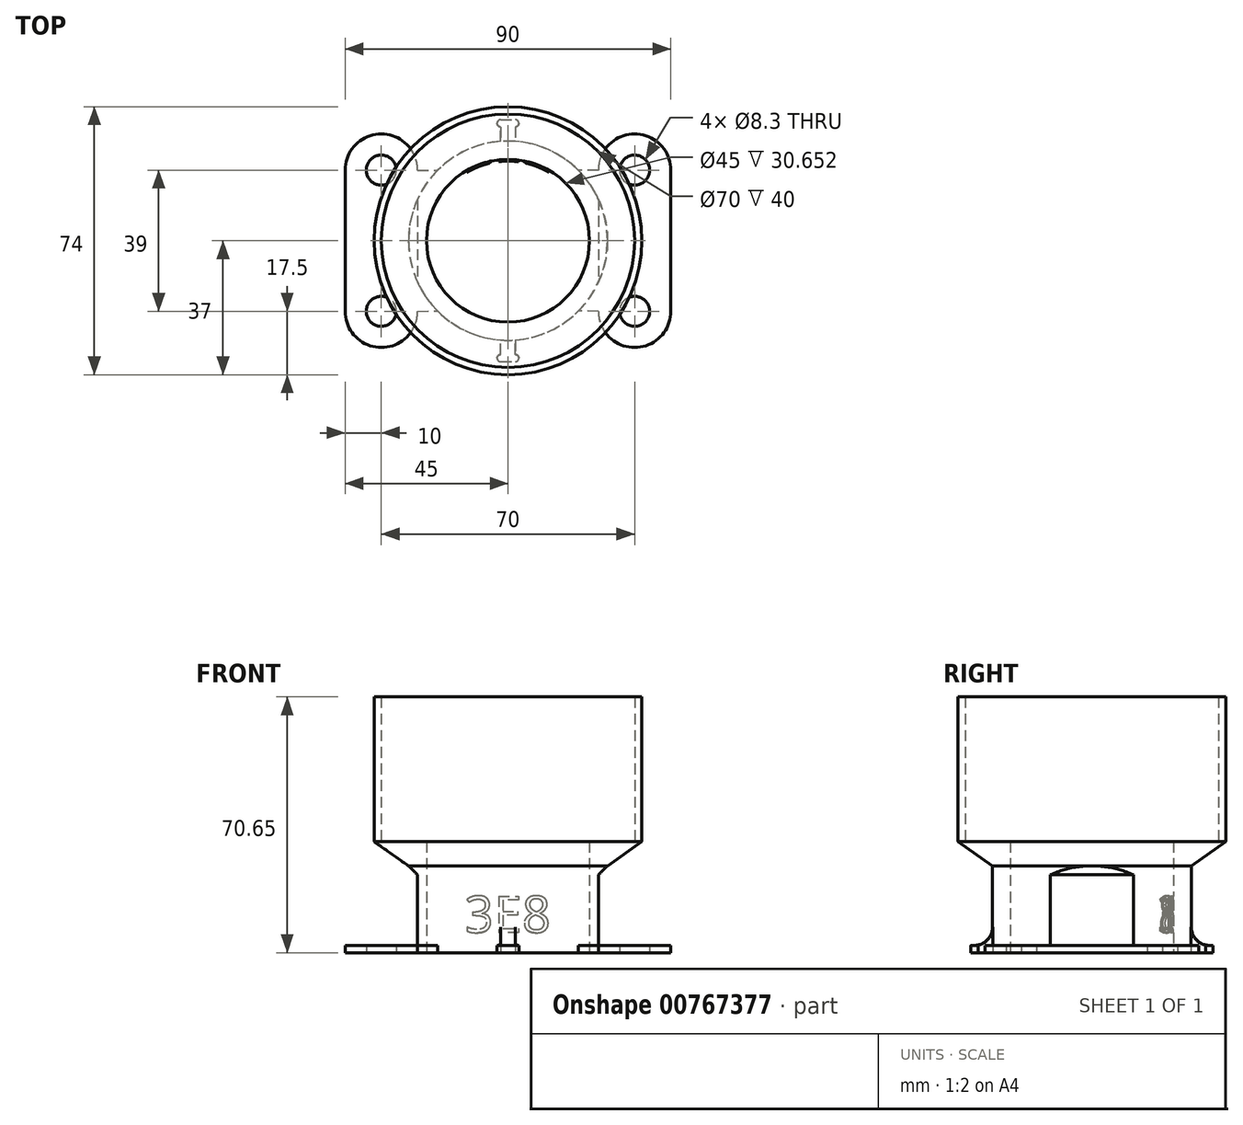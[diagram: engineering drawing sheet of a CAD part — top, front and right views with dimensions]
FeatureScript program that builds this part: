
annotation { "Feature Type Name" : "Feature", "Feature Type Description" : "" }
export const myFeature = defineFeature(function(context is Context, id is Id, definition is map)
    precondition{}
    {
        {
            assignVariable(context, id + "F0", {"name" : "mountheight", "anyValue" : 22});
        }
        {
            assignVariable(context, id + "F1", {"name" : "cupholderdepth", "anyValue" : 40});
        }
        {
            var Q0;
            Q0=qCreatedBy(makeId("Top.planeOp"),FACE);
            var sketch = newSketch(context, id + "F2", { "sketchPlane" : qUnion([Q0])});
            skLineSegment(sketch, "E0", {"start": v(-35, 0) * mm, "end": v(35, 0) * mm, "construction": true});
            skLineSegment(sketch, "E1", {"start": v(0, 27.5) * mm, "end": v(0, 0) * mm, "construction": true});
            skLineSegment(sketch, "E2", {"start": v(-35, 19.5) * mm, "end": v(-35, -19.5) * mm, "construction": true});
            skCircle(sketch, "E3", {"center": v(-35, 19.5) * mm, "radius": 4.15 * mm});
            skCircle(sketch, "E4.MirrorC", {"center": v(-35, -19.5) * mm, "radius": 4.15 * mm});
            skCircle(sketch, "E5.MirrorC", {"center": v(35, 19.5) * mm, "radius": 4.15 * mm});
            skCircle(sketch, "E6.MirrorC", {"center": v(35, -19.5) * mm, "radius": 4.15 * mm});
            skCircle(sketch, "E7", {"center": v(-35, 19.5) * mm, "radius": 10 * mm, "construction": true});
            skCircle(sketch, "E8.MirrorC", {"center": v(-35, -19.5) * mm, "radius": 10 * mm, "construction": true});
            skLineSegment(sketch, "E9", {"start": v(-45, 19.5) * mm, "end": v(-35, 19.5) * mm, "construction": true});
            skLineSegment(sketch, "E10", {"start": v(-35, -19.5) * mm, "end": v(-45, -19.5) * mm, "construction": true});
            skLineSegment(sketch, "E11", {"start": v(0, 0) * mm, "end": v(-19.45, 19.45) * mm, "construction": true});
            skLineSegment(sketch, "E12", {"start": v(-35, 19.5) * mm, "end": v(-35, 29.5) * mm, "construction": true});
            skArc(sketch, "E13", {"start": v(-25, 19.5) * mm, "mid": v(-35, 29.5) * mm, "end": v(-45, 19.5) * mm});
            skArc(sketch, "E14.MirrorCS", {"start": v(25, 19.5) * mm, "mid": v(35, 29.5) * mm, "end": v(45, 19.5) * mm});
            skArc(sketch, "E15.MirrorCS", {"start": v(25, -19.5) * mm, "mid": v(35, -29.5) * mm, "end": v(45, -19.5) * mm});
            skArc(sketch, "E16.MirrorCS", {"start": v(-25, -19.5) * mm, "mid": v(-35, -29.5) * mm, "end": v(-45, -19.5) * mm});
            skLineSegment(sketch, "E17", {"start": v(-25, 19.5) * mm, "end": v(-25, -19.5) * mm, "construction": true});
            skLineSegment(sketch, "E18", {"start": v(-45, 19.5) * mm, "end": v(-45, -19.5) * mm});
            skLineSegment(sketch, "E19.MirrorCS", {"start": v(45, 19.5) * mm, "end": v(45, -19.5) * mm});
            skCircle(sketch, "E20", {"center": v(0, 0) * mm, "radius": 22.5 * mm});
            skCircle(sketch, "E21.0", {"center": v(0, 0) * mm, "radius": 27.5 * mm});
            skLineSegment(sketch, "E22", {"start": v(-25, 19.5) * mm, "end": v(-19.45, 19.45) * mm});
            skLineSegment(sketch, "E23.MirrorCS", {"start": v(-25, -19.5) * mm, "end": v(-19.45, -19.45) * mm});
            skLineSegment(sketch, "E24.MirrorCS", {"start": v(25, 19.5) * mm, "end": v(19.45, 19.45) * mm});
            skLineSegment(sketch, "E25.MirrorCS", {"start": v(25, -19.5) * mm, "end": v(19.45, -19.45) * mm});
            skLineSegment(sketch, "E26.bottom", {"start": v(-2, 27.43) * mm, "end": v(2, 27.43) * mm, "construction": true});
            skLineSegment(sketch, "E26.top", {"start": v(-2, 33.43) * mm, "end": v(2, 33.43) * mm});
            skLineSegment(sketch, "E26.left", {"start": v(-2, 27.43) * mm, "end": v(-2, 33.43) * mm, "construction": true});
            skLineSegment(sketch, "E26.right", {"start": v(2, 27.43) * mm, "end": v(2, 33.43) * mm, "construction": true});
            skArc(sketch, "E27", {"start": v(-2, 33.43) * mm, "mid": v(-3, 32.43) * mm, "end": v(-2, 31.43) * mm});
            skArc(sketch, "E28.MirrorCS", {"start": v(2, 33.43) * mm, "mid": v(3, 32.43) * mm, "end": v(2, 31.43) * mm});
            skLineSegment(sketch, "E29", {"start": v(-2, 31.43) * mm, "end": v(-2, 27.43) * mm});
            skLineSegment(sketch, "E30", {"start": v(2, 31.43) * mm, "end": v(2, 27.43) * mm});
            skLineSegment(sketch, "E31.MirrorCS", {"start": v(-2, -31.43) * mm, "end": v(-2, -27.43) * mm});
            skArc(sketch, "E32.MirrorCS", {"start": v(-2, -33.43) * mm, "mid": v(-3, -32.43) * mm, "end": v(-2, -31.43) * mm});
            skLineSegment(sketch, "E33.MirrorCS", {"start": v(-2, -33.43) * mm, "end": v(2, -33.43) * mm});
            skArc(sketch, "E34.MirrorCS", {"start": v(2, -33.43) * mm, "mid": v(3, -32.43) * mm, "end": v(2, -31.43) * mm});
            skLineSegment(sketch, "E35.MirrorCS", {"start": v(2, -31.43) * mm, "end": v(2, -27.43) * mm});
            skSolve(sketch);
        }
        {
            var Q0;
            Q0 = qSketchRegion(id + "F2", true);
            extrude(context, id + "F3", {"entities" : qUnion([Q0]), "depth" : 2 * mm, "offsetDistance" : 25 * mm});
        }
        {
            var Q0;
            Q0=makeQuery(id+"F3.opExtrude","CAP_FACE",FACE,{"disambiguationData":[OSD([sQuery(id+"F2.wireOp",EDGE,"E3"),sQuery(id+"F2.wireOp",EDGE,"E4.MirrorC"),sQuery(id+"F2.wireOp",EDGE,"E5.MirrorC"),sQuery(id+"F2.wireOp",EDGE,"E6.MirrorC"),sQuery(id+"F2.wireOp",EDGE,"E13"),sQuery(id+"F2.wireOp",EDGE,"E14.MirrorCS"),sQuery(id+"F2.wireOp",EDGE,"E15.MirrorCS"),sQuery(id+"F2.wireOp",EDGE,"E16.MirrorCS"),sQuery(id+"F2.wireOp",EDGE,"7Ii40RzH-jyae-TEvV-coND-dObG0fQAQXqJ"),sQuery(id+"F2.wireOp",EDGE,"UbCVeuCc-5SeI-YLZf-K4XL-lkeGF2V2fitj"),sQuery(id+"F2.wireOp",EDGE,"E18"),sQuery(id+"F2.wireOp",EDGE,"E19.MirrorCS"),sQuery(id+"F2.wireOp",EDGE,"da887730-7b05-43a9-8dbc-d6b6659f2c340.MirrorCS")])],"isStart":false});
            var sketch = newSketch(context, id + "F4", { "sketchPlane" : qUnion([Q0])});
            skCircle(sketch, "E36.0", {"center": v(0, 0) * mm, "radius": 27.5 * mm});
            skPoint(sketch, "E37.0", {"position": v(25, 19.5) * mm});
            skCircle(sketch, "E38.0", {"center": v(0, 0) * mm, "radius": 22.5 * mm});
            skSolve(sketch);
        }
        {
            var Q0;
            Q0 = qSketchRegion(id + "F4", true);
            extrude(context, id + "F5", {"entities" : qUnion([Q0]), "operationType" : NewBodyOperationType.ADD, "depth" : (getVariable(context, 'mountheight')) * mm, "offsetDistance" : 25 * mm});
        }
        {
            var Q0;
            Q0=qCreatedBy(makeId("Front.planeOp"),FACE);
            var sketch = newSketch(context, id + "F6", { "sketchPlane" : qUnion([Q0])});
            skLineSegment(sketch, "E39", {"start": v(0, 0) * mm, "end": v(0, 30.65) * mm, "construction": true});
            skLineSegment(sketch, "E40", {"start": v(0, 30.65) * mm, "end": v(37, 30.65) * mm, "construction": true});
            skLineSegment(sketch, "E41.0", {"start": v(-27.5, 24) * mm, "end": v(27.5, 24) * mm, "construction": true});
            skLineSegment(sketch, "E42.0", {"start": v(-22.5, 24) * mm, "end": v(22.5, 24) * mm, "construction": true});
            skLineSegment(sketch, "E43", {"start": v(22.5, 24) * mm, "end": v(27.5, 24) * mm});
            skLineSegment(sketch, "E44", {"start": v(37, 30.65) * mm, "end": v(27.5, 24) * mm});
            skLineSegment(sketch, "E45", {"start": v(37, 30.65) * mm, "end": v(22.5, 30.65) * mm});
            skLineSegment(sketch, "E46", {"start": v(22.5, 30.65) * mm, "end": v(22.5, 24) * mm});
            skSolve(sketch);
        }
        {
            var Q0;
            Q0 = qSketchRegion(id + "F6", true);
            var Q1;
            Q1=sQuery(id+"F6.wireOp",EDGE,"E39");
            revolve(context, id + "F7", {"operationType" : NewBodyOperationType.ADD, "surfaceOperationType" : NewSurfaceOperationType.NEW, "entities" : qUnion([Q0]), "axis" : qUnion([Q1]), "revolveType" : RevolveType.FULL});
        }
        {
            var Q0;
            Q0=makeQuery(id+"F7.opRevolve","SWEPT_FACE",FACE,{"disambiguationData":[OSD([sQuery(id+"F6.wireOp",EDGE,"E45")])]});
            var sketch = newSketch(context, id + "F8", { "sketchPlane" : qUnion([Q0])});
            skCircle(sketch, "E47.0", {"center": v(0, 0) * mm, "radius": 37 * mm});
            skCircle(sketch, "E48.0", {"center": v(0, 0) * mm, "radius": 35 * mm});
            skSolve(sketch);
        }
        {
            var Q0;
            Q0 = qSketchRegion(id + "F8", true);
            extrude(context, id + "F9", {"entities" : qUnion([Q0]), "operationType" : NewBodyOperationType.ADD, "depth" : (getVariable(context, 'cupholderdepth')) * mm, "offsetDistance" : 25 * mm});
        }
        {
            var Q0;
            {var subQ2=sQuery(id+"F2.wireOp",EDGE,"E31.MirrorCS");var subQ9=sQuery(id+"F4.wireOp",EDGE,"E36.0");Q0=makeQuery(id+"F5.boolean.opBoolean","SPLIT",EDGE,{"disambiguationData":[TD([makeQuery(id+"F3.opExtrude","SWEPT_FACE",FACE,{"disambiguationData":[OSD([subQ2])]})])],"derivedFrom":makeQuery(id+"F5.opExtrude","CAP_EDGE",EDGE,{"disambiguationData":[OSD([subQ9])],"isStart":true})});}
            var Q1;
            {var subQ4=sQuery(id+"F2.wireOp",EDGE,"E29");var subQ9=sQuery(id+"F4.wireOp",EDGE,"E36.0");Q1=makeQuery(id+"F5.boolean.opBoolean","SPLIT",EDGE,{"disambiguationData":[TD([makeQuery(id+"F3.opExtrude","SWEPT_FACE",FACE,{"disambiguationData":[OSD([subQ4])]})])],"derivedFrom":makeQuery(id+"F5.opExtrude","CAP_EDGE",EDGE,{"disambiguationData":[OSD([subQ9])],"isStart":true})});}
            fillet(context, id + "F10", {"entities" : qUnion([Q0, Q1]), "radius" : 5 * mm, "tangentPropagation" : true, "allowEdgeOverflow" : false});
        }
        {
            var Q0;
            Q0=qCreatedBy(makeId("Front.planeOp"),FACE);
            var sketch = newSketch(context, id + "F11", { "sketchPlane" : qUnion([Q0])});
            skLineSegment(sketch, "E49", {"start": v(-22.5, 0) * mm, "end": v(-22.5, 24.96) * mm, "construction": true});
            skLineSegment(sketch, "E50", {"start": v(22.5, 28.65) * mm, "end": v(22.5, -3.69) * mm, "construction": true});
            skLineSegment(sketch, "E51", {"start": v(-22.5, 24.96) * mm, "end": v(22.5, -3.69) * mm, "construction": true});
            skText(sketch, "E52", { "text": "3E8", "fontName": "OpenSans-Regular.ttf"});
            skPoint(sketch, "E53", {"position": v(0, 10.64) * mm});
            const initialGuessF11  = {"E52": [-0.012, 0.0056, 1, 0, 0.0101]};
            skSetInitialGuess(sketch, initialGuessF11);
            skSolve(sketch);
        }
        {
            var Q0;
            Q0 = qSketchRegion(id + "F11", true);
            var Q1;
            Q1=makeQuery(id+"F7.boolean.opBoolean","MERGE",FACE,{"derivedFrom":[makeQuery(id+"F5.boolean.opBoolean","MERGE",FACE,{"derivedFrom":[makeQuery(id+"F3.opExtrude","SWEPT_FACE",FACE,{"disambiguationData":[OSD([sQuery(id+"F2.wireOp",EDGE,"E20")])]}),makeQuery(id+"F5.opExtrude","SWEPT_FACE",FACE,{"disambiguationData":[OSD([sQuery(id+"F4.wireOp",EDGE,"E38.0")])]})]}),makeQuery(id+"F7.opRevolve","SWEPT_FACE",FACE,{"disambiguationData":[OSD([sQuery(id+"F6.wireOp",EDGE,"E46")])]})]});
            extrude(context, id + "F12", {"entities" : qUnion([Q0]), "operationType" : NewBodyOperationType.ADD, "endBound" : BoundingType.UP_TO_SURFACE, "oppositeDirection" : true, "depth" : 25 * mm, "endBoundEntityFace" : qUnion([Q1]), "offsetDistance" : 25 * mm});
        }
        {
            var Q0;
            Q0=makeQuery(id+"F7.opRevolve","SWEPT_FACE",FACE,{"disambiguationData":[OSD([sQuery(id+"F6.wireOp",EDGE,"E45")])]});
            var sketch = newSketch(context, id + "F13", { "sketchPlane" : qUnion([Q0])});
            skCircle(sketch, "E54.0", {"center": v(0, 0) * mm, "radius": 22 * mm});
            skSolve(sketch);
        }
        {
            var Q0;
            Q0 = qSketchRegion(id + "F13", true);
            extrude(context, id + "F14", {"entities" : qUnion([Q0]), "operationType" : NewBodyOperationType.REMOVE, "endBound" : BoundingType.THROUGH_ALL, "oppositeDirection" : true, "depth" : 25 * mm, "offsetDistance" : 25 * mm});
        }
        {
            var Q0;
            Q0=qCreatedBy(makeId("Front.planeOp"),FACE);
            var sketch = newSketch(context, id + "F15", { "sketchPlane" : qUnion([Q0])});
            skPoint(sketch, "E55.0", {"position": v(25, 2) * mm});
            skPoint(sketch, "E56.0", {"position": v(-25, 2) * mm});
            skLineSegment(sketch, "E57", {"start": v(27.5, 24) * mm, "end": v(27.5, 2) * mm});
            skLineSegment(sketch, "E58.0", {"start": v(0, 0) * mm, "end": v(0, 30.65) * mm, "construction": true});
            skLineSegment(sketch, "E59", {"start": v(25, 2) * mm, "end": v(27.5, 2) * mm});
            skLineSegment(sketch, "E60", {"start": v(25, 2) * mm, "end": v(25, 21.5) * mm});
            skLineSegment(sketch, "E61", {"start": v(25, 21.5) * mm, "end": v(27.5, 24) * mm});
            skLineSegment(sketch, "E62.MirrorCS", {"start": v(-25, 2) * mm, "end": v(-27.5, 2) * mm});
            skLineSegment(sketch, "E63.MirrorCS", {"start": v(-27.5, 24) * mm, "end": v(-27.5, 2) * mm});
            skLineSegment(sketch, "E64.MirrorCS", {"start": v(-25, 21.5) * mm, "end": v(-27.5, 24) * mm});
            skLineSegment(sketch, "E65.MirrorCS", {"start": v(-25, 2) * mm, "end": v(-25, 21.5) * mm});
            skSolve(sketch);
        }
        {
            var Q0;
            Q0 = qSketchRegion(id + "F15", true);
            extrude(context, id + "F16", {"entities" : qUnion([Q0]), "operationType" : NewBodyOperationType.REMOVE, "endBound" : BoundingType.THROUGH_ALL, "oppositeDirection" : true, "depth" : 25 * mm, "offsetDistance" : 25 * mm, "hasSecondDirection" : true, "secondDirectionBound" : SecondDirectionBoundingType.THROUGH_ALL, "secondDirectionOppositeDirection" : false, "secondDirectionDepth" : 25 * mm});
        }
    });
